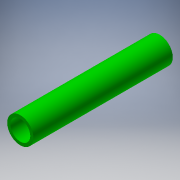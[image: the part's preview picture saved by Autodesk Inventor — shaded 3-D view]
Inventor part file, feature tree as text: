
AUTODESK INVENTOR PART (.ipt)
format: ipt  version: 2018.2 (Build 222227000, 227)  size: 109,056 bytes
history: native  units: in
note: dims shown in document units (in); Inventor stores cm internally (conversion verified against a paired STEP export)
features: extrude x1, sketch x1
ambient origin geometry x8: Origin, YZ Plane, XZ Plane, XY Plane, X Axis, Y Axis, Z Axis, Center Point
bodies: Solid1 (feature_tree)
feature tree (2):
  extrude  "Extrusion1"  Depth=7.0in
  sketch  "Sketch1"  dims[d0=1.315in d1=1.0in d2=7.0in d3=0.0in]
